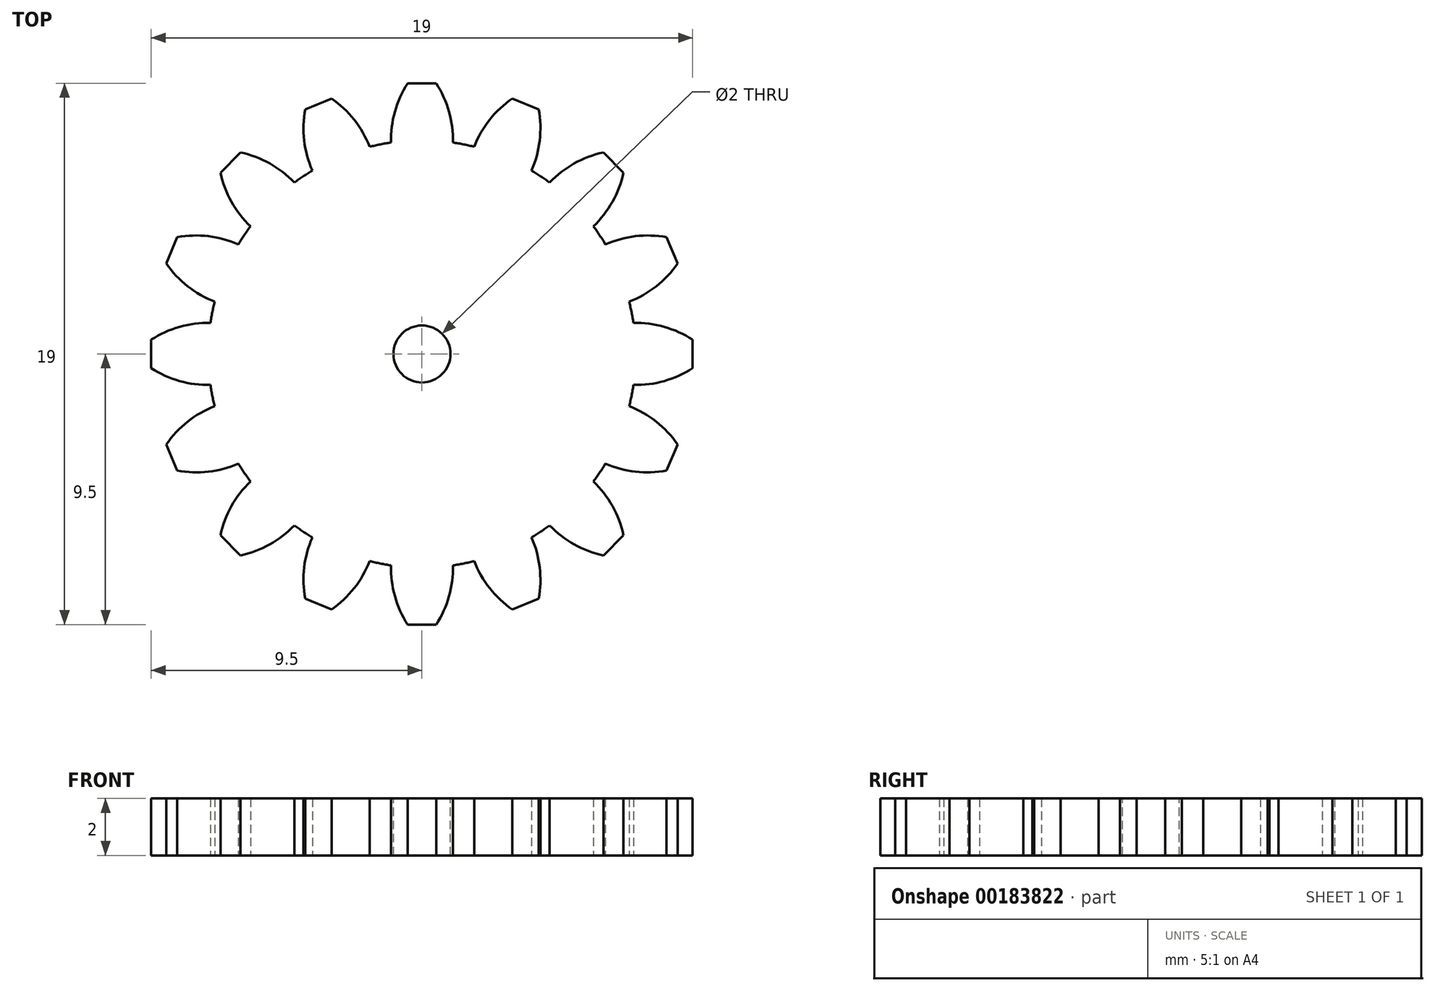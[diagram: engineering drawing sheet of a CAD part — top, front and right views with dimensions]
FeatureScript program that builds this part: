
annotation { "Feature Type Name" : "Feature", "Feature Type Description" : "" }
export const myFeature = defineFeature(function(context is Context, id is Id, definition is map)
    precondition{}
    {
        {
            var Q0;
            Q0=qCreatedBy(makeId("Top.planeOp"),FACE);
            var sketch = newSketch(context, id + "F0", { "sketchPlane" : qUnion([Q0])});
            skCircle(sketch, "E0", {"center": v(0, 0) * mm, "radius": 7.5 * mm});
            skLineSegment(sketch, "E1", {"start": v(0, 0) * mm, "end": v(0, 7.5) * mm, "construction": true});
            skLineSegment(sketch, "E2", {"start": v(0, 9.5) * mm, "end": v(-0.5, 9.5) * mm});
            skArc(sketch, "E3", {"start": v(-0.5, 9.5) * mm, "mid": v(-0.95, 8.5) * mm, "end": v(-1.09, 7.42) * mm});
            skLineSegment(sketch, "E4.MirrorCS", {"start": v(0, 9.5) * mm, "end": v(0.5, 9.5) * mm});
            skArc(sketch, "E5.MirrorCS", {"start": v(0.5, 9.5) * mm, "mid": v(0.95, 8.5) * mm, "end": v(1.09, 7.42) * mm});
            skLineSegment(sketch, "E6.1.0", {"start": v(-3.64, 8.78) * mm, "end": v(-4.1, 8.59) * mm});
            skArc(sketch, "E6.1.1", {"start": v(-4.1, 8.59) * mm, "mid": v(-4.13, 7.5) * mm, "end": v(-3.85, 6.44) * mm});
            skLineSegment(sketch, "E6.1.2", {"start": v(-3.64, 8.78) * mm, "end": v(-3.17, 8.97) * mm});
            skArc(sketch, "E6.1.3", {"start": v(-3.17, 8.97) * mm, "mid": v(-2.38, 8.22) * mm, "end": v(-1.83, 7.27) * mm});
            skLineSegment(sketch, "E6.2.0", {"start": v(-6.72, 6.72) * mm, "end": v(-7.07, 6.36) * mm});
            skArc(sketch, "E6.2.1", {"start": v(-7.07, 6.36) * mm, "mid": v(-6.69, 5.34) * mm, "end": v(-6.02, 4.48) * mm});
            skLineSegment(sketch, "E6.2.2", {"start": v(-6.72, 6.72) * mm, "end": v(-6.36, 7.07) * mm});
            skArc(sketch, "E6.2.3", {"start": v(-6.36, 7.07) * mm, "mid": v(-5.34, 6.69) * mm, "end": v(-4.48, 6.02) * mm});
            skLineSegment(sketch, "E6.3.0", {"start": v(-8.78, 3.64) * mm, "end": v(-8.97, 3.17) * mm});
            skArc(sketch, "E6.3.1", {"start": v(-8.97, 3.17) * mm, "mid": v(-8.22, 2.38) * mm, "end": v(-7.27, 1.83) * mm});
            skLineSegment(sketch, "E6.3.2", {"start": v(-8.78, 3.64) * mm, "end": v(-8.59, 4.1) * mm});
            skArc(sketch, "E6.3.3", {"start": v(-8.59, 4.1) * mm, "mid": v(-7.5, 4.13) * mm, "end": v(-6.44, 3.85) * mm});
            skLineSegment(sketch, "E6.4.0", {"start": v(-9.5, 0) * mm, "end": v(-9.5, -0.5) * mm});
            skArc(sketch, "E6.4.1", {"start": v(-9.5, -0.5) * mm, "mid": v(-8.5, -0.95) * mm, "end": v(-7.42, -1.09) * mm});
            skLineSegment(sketch, "E6.4.2", {"start": v(-9.5, 0) * mm, "end": v(-9.5, 0.5) * mm});
            skArc(sketch, "E6.4.3", {"start": v(-9.5, 0.5) * mm, "mid": v(-8.5, 0.95) * mm, "end": v(-7.42, 1.09) * mm});
            skLineSegment(sketch, "E6.5.0", {"start": v(-8.78, -3.64) * mm, "end": v(-8.59, -4.1) * mm});
            skArc(sketch, "E6.5.1", {"start": v(-8.59, -4.1) * mm, "mid": v(-7.5, -4.13) * mm, "end": v(-6.44, -3.85) * mm});
            skLineSegment(sketch, "E6.5.2", {"start": v(-8.78, -3.64) * mm, "end": v(-8.97, -3.17) * mm});
            skArc(sketch, "E6.5.3", {"start": v(-8.97, -3.17) * mm, "mid": v(-8.22, -2.38) * mm, "end": v(-7.27, -1.83) * mm});
            skLineSegment(sketch, "E6.6.0", {"start": v(-6.72, -6.72) * mm, "end": v(-6.36, -7.07) * mm});
            skArc(sketch, "E6.6.1", {"start": v(-6.36, -7.07) * mm, "mid": v(-5.34, -6.69) * mm, "end": v(-4.48, -6.02) * mm});
            skLineSegment(sketch, "E6.6.2", {"start": v(-6.72, -6.72) * mm, "end": v(-7.07, -6.36) * mm});
            skArc(sketch, "E6.6.3", {"start": v(-7.07, -6.36) * mm, "mid": v(-6.69, -5.34) * mm, "end": v(-6.02, -4.48) * mm});
            skLineSegment(sketch, "E6.7.0", {"start": v(-3.64, -8.78) * mm, "end": v(-3.17, -8.97) * mm});
            skArc(sketch, "E6.7.1", {"start": v(-3.17, -8.97) * mm, "mid": v(-2.38, -8.22) * mm, "end": v(-1.83, -7.27) * mm});
            skLineSegment(sketch, "E6.7.2", {"start": v(-3.64, -8.78) * mm, "end": v(-4.1, -8.59) * mm});
            skArc(sketch, "E6.7.3", {"start": v(-4.1, -8.59) * mm, "mid": v(-4.13, -7.5) * mm, "end": v(-3.85, -6.44) * mm});
            skLineSegment(sketch, "E6.8.0", {"start": v(0, -9.5) * mm, "end": v(0.5, -9.5) * mm});
            skArc(sketch, "E6.8.1", {"start": v(0.5, -9.5) * mm, "mid": v(0.95, -8.5) * mm, "end": v(1.09, -7.42) * mm});
            skLineSegment(sketch, "E6.8.2", {"start": v(0, -9.5) * mm, "end": v(-0.5, -9.5) * mm});
            skArc(sketch, "E6.8.3", {"start": v(-0.5, -9.5) * mm, "mid": v(-0.95, -8.5) * mm, "end": v(-1.09, -7.42) * mm});
            skLineSegment(sketch, "E6.9.0", {"start": v(3.64, -8.78) * mm, "end": v(4.1, -8.59) * mm});
            skArc(sketch, "E6.9.1", {"start": v(4.1, -8.59) * mm, "mid": v(4.13, -7.5) * mm, "end": v(3.85, -6.44) * mm});
            skLineSegment(sketch, "E6.9.2", {"start": v(3.64, -8.78) * mm, "end": v(3.17, -8.97) * mm});
            skArc(sketch, "E6.9.3", {"start": v(3.17, -8.97) * mm, "mid": v(2.38, -8.22) * mm, "end": v(1.83, -7.27) * mm});
            skLineSegment(sketch, "E6.10.0", {"start": v(6.72, -6.72) * mm, "end": v(7.07, -6.36) * mm});
            skArc(sketch, "E6.10.1", {"start": v(7.07, -6.36) * mm, "mid": v(6.69, -5.34) * mm, "end": v(6.02, -4.48) * mm});
            skLineSegment(sketch, "E6.10.2", {"start": v(6.72, -6.72) * mm, "end": v(6.36, -7.07) * mm});
            skArc(sketch, "E6.10.3", {"start": v(6.36, -7.07) * mm, "mid": v(5.34, -6.69) * mm, "end": v(4.48, -6.02) * mm});
            skLineSegment(sketch, "E6.11.0", {"start": v(8.78, -3.64) * mm, "end": v(8.97, -3.17) * mm});
            skArc(sketch, "E6.11.1", {"start": v(8.97, -3.17) * mm, "mid": v(8.22, -2.38) * mm, "end": v(7.27, -1.83) * mm});
            skLineSegment(sketch, "E6.11.2", {"start": v(8.78, -3.64) * mm, "end": v(8.59, -4.1) * mm});
            skArc(sketch, "E6.11.3", {"start": v(8.59, -4.1) * mm, "mid": v(7.5, -4.13) * mm, "end": v(6.44, -3.85) * mm});
            skLineSegment(sketch, "E6.12.0", {"start": v(9.5, 0) * mm, "end": v(9.5, 0.5) * mm});
            skArc(sketch, "E6.12.1", {"start": v(9.5, 0.5) * mm, "mid": v(8.5, 0.95) * mm, "end": v(7.42, 1.09) * mm});
            skLineSegment(sketch, "E6.12.2", {"start": v(9.5, 0) * mm, "end": v(9.5, -0.5) * mm});
            skArc(sketch, "E6.12.3", {"start": v(9.5, -0.5) * mm, "mid": v(8.5, -0.95) * mm, "end": v(7.42, -1.09) * mm});
            skLineSegment(sketch, "E6.13.0", {"start": v(8.78, 3.64) * mm, "end": v(8.59, 4.1) * mm});
            skArc(sketch, "E6.13.1", {"start": v(8.59, 4.1) * mm, "mid": v(7.5, 4.13) * mm, "end": v(6.44, 3.85) * mm});
            skLineSegment(sketch, "E6.13.2", {"start": v(8.78, 3.64) * mm, "end": v(8.97, 3.17) * mm});
            skArc(sketch, "E6.13.3", {"start": v(8.97, 3.17) * mm, "mid": v(8.22, 2.38) * mm, "end": v(7.27, 1.83) * mm});
            skLineSegment(sketch, "E6.14.0", {"start": v(6.72, 6.72) * mm, "end": v(6.36, 7.07) * mm});
            skArc(sketch, "E6.14.1", {"start": v(6.36, 7.07) * mm, "mid": v(5.34, 6.69) * mm, "end": v(4.48, 6.02) * mm});
            skLineSegment(sketch, "E6.14.2", {"start": v(6.72, 6.72) * mm, "end": v(7.07, 6.36) * mm});
            skArc(sketch, "E6.14.3", {"start": v(7.07, 6.36) * mm, "mid": v(6.69, 5.34) * mm, "end": v(6.02, 4.48) * mm});
            skLineSegment(sketch, "E6.15.0", {"start": v(3.64, 8.78) * mm, "end": v(3.17, 8.97) * mm});
            skArc(sketch, "E6.15.1", {"start": v(3.17, 8.97) * mm, "mid": v(2.38, 8.22) * mm, "end": v(1.83, 7.27) * mm});
            skLineSegment(sketch, "E6.15.2", {"start": v(3.64, 8.78) * mm, "end": v(4.1, 8.59) * mm});
            skArc(sketch, "E6.15.3", {"start": v(4.1, 8.59) * mm, "mid": v(4.13, 7.5) * mm, "end": v(3.85, 6.44) * mm});
            skSolve(sketch);
        }
        {
            var Q0;
            Q0 = qSketchRegion(id + "F0", true);
            extrude(context, id + "F1", {"entities" : qUnion([Q0]), "depth" : 2 * mm});
        }
        {
            var Q0;
            Q0=makeQuery(id+"F1.opExtrude","CAP_FACE",FACE,{"disambiguationData":[OSD([sQuery(id+"F0.wireOp",EDGE,"E0"),sQuery(id+"F0.wireOp",EDGE,"E2"),sQuery(id+"F0.wireOp",EDGE,"E3"),sQuery(id+"F0.wireOp",EDGE,"E4.MirrorCS"),sQuery(id+"F0.wireOp",EDGE,"E5.MirrorCS"),sQuery(id+"F0.wireOp",EDGE,"E6.1.0"),sQuery(id+"F0.wireOp",EDGE,"E6.1.1"),sQuery(id+"F0.wireOp",EDGE,"E6.1.2"),sQuery(id+"F0.wireOp",EDGE,"E6.1.3"),sQuery(id+"F0.wireOp",EDGE,"E6.2.0"),sQuery(id+"F0.wireOp",EDGE,"E6.2.1"),sQuery(id+"F0.wireOp",EDGE,"E6.2.2"),sQuery(id+"F0.wireOp",EDGE,"E6.2.3"),sQuery(id+"F0.wireOp",EDGE,"E6.3.0"),sQuery(id+"F0.wireOp",EDGE,"E6.3.1"),sQuery(id+"F0.wireOp",EDGE,"E6.3.2"),sQuery(id+"F0.wireOp",EDGE,"E6.3.3"),sQuery(id+"F0.wireOp",EDGE,"E6.4.0"),sQuery(id+"F0.wireOp",EDGE,"E6.4.1"),sQuery(id+"F0.wireOp",EDGE,"E6.4.2"),sQuery(id+"F0.wireOp",EDGE,"E6.4.3"),sQuery(id+"F0.wireOp",EDGE,"E6.5.0"),sQuery(id+"F0.wireOp",EDGE,"E6.5.1"),sQuery(id+"F0.wireOp",EDGE,"E6.5.2"),sQuery(id+"F0.wireOp",EDGE,"E6.5.3"),sQuery(id+"F0.wireOp",EDGE,"E6.6.0"),sQuery(id+"F0.wireOp",EDGE,"E6.6.1"),sQuery(id+"F0.wireOp",EDGE,"E6.6.2"),sQuery(id+"F0.wireOp",EDGE,"E6.6.3"),sQuery(id+"F0.wireOp",EDGE,"E6.7.0"),sQuery(id+"F0.wireOp",EDGE,"E6.7.1"),sQuery(id+"F0.wireOp",EDGE,"E6.7.2"),sQuery(id+"F0.wireOp",EDGE,"E6.7.3"),sQuery(id+"F0.wireOp",EDGE,"E6.8.0"),sQuery(id+"F0.wireOp",EDGE,"E6.8.1"),sQuery(id+"F0.wireOp",EDGE,"E6.8.2"),sQuery(id+"F0.wireOp",EDGE,"E6.8.3"),sQuery(id+"F0.wireOp",EDGE,"E6.9.0"),sQuery(id+"F0.wireOp",EDGE,"E6.9.1"),sQuery(id+"F0.wireOp",EDGE,"E6.9.2"),sQuery(id+"F0.wireOp",EDGE,"E6.9.3"),sQuery(id+"F0.wireOp",EDGE,"E6.10.0"),sQuery(id+"F0.wireOp",EDGE,"E6.10.1"),sQuery(id+"F0.wireOp",EDGE,"E6.10.2"),sQuery(id+"F0.wireOp",EDGE,"E6.10.3"),sQuery(id+"F0.wireOp",EDGE,"E6.11.0"),sQuery(id+"F0.wireOp",EDGE,"E6.11.1"),sQuery(id+"F0.wireOp",EDGE,"E6.11.2"),sQuery(id+"F0.wireOp",EDGE,"E6.11.3"),sQuery(id+"F0.wireOp",EDGE,"E6.12.0"),sQuery(id+"F0.wireOp",EDGE,"E6.12.1"),sQuery(id+"F0.wireOp",EDGE,"E6.12.2"),sQuery(id+"F0.wireOp",EDGE,"E6.12.3"),sQuery(id+"F0.wireOp",EDGE,"E6.13.0"),sQuery(id+"F0.wireOp",EDGE,"E6.13.1"),sQuery(id+"F0.wireOp",EDGE,"E6.13.2"),sQuery(id+"F0.wireOp",EDGE,"E6.13.3"),sQuery(id+"F0.wireOp",EDGE,"E6.14.0"),sQuery(id+"F0.wireOp",EDGE,"E6.14.1"),sQuery(id+"F0.wireOp",EDGE,"E6.14.2"),sQuery(id+"F0.wireOp",EDGE,"E6.14.3"),sQuery(id+"F0.wireOp",EDGE,"E6.15.0"),sQuery(id+"F0.wireOp",EDGE,"E6.15.1"),sQuery(id+"F0.wireOp",EDGE,"E6.15.2"),sQuery(id+"F0.wireOp",EDGE,"E6.15.3")])],"isStart":false});
            var sketch = newSketch(context, id + "F2", { "sketchPlane" : qUnion([Q0])});
            skCircle(sketch, "E7", {"center": v(0, 0) * mm, "radius": 1 * mm});
            skSolve(sketch);
        }
        {
            var Q0;
            Q0 = qSketchRegion(id + "F2", true);
            extrude(context, id + "F3", {"entities" : qUnion([Q0]), "operationType" : NewBodyOperationType.REMOVE, "endBound" : BoundingType.THROUGH_ALL, "oppositeDirection" : true, "depth" : 25 * mm});
        }
    });
